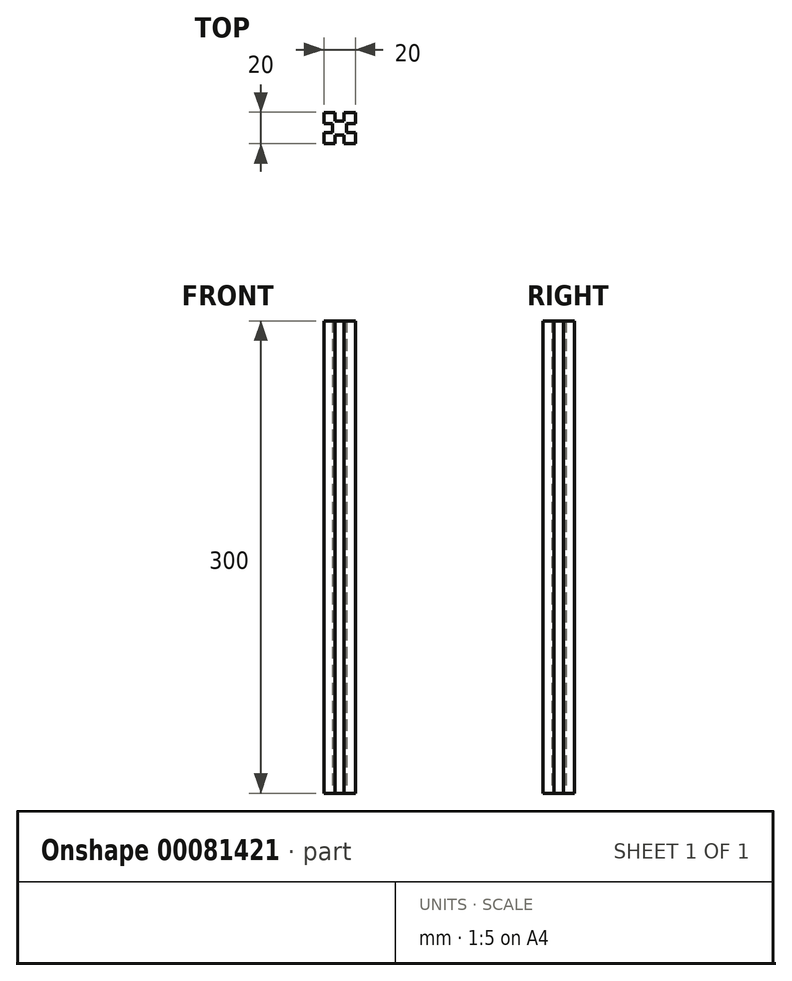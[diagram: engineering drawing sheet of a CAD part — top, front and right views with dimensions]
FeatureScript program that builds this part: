
annotation { "Feature Type Name" : "Feature", "Feature Type Description" : "" }
export const myFeature = defineFeature(function(context is Context, id is Id, definition is map)
    precondition{}
    {
        {
            var Q0;
            Q0=qCreatedBy(makeId("Top.planeOp"),FACE);
            var sketch = newSketch(context, id + "F0", { "sketchPlane" : qUnion([Q0])});
            skLineSegment(sketch, "E0.bottom", {"start": v(-87.17, -55.96) * mm, "end": v(-67.17, -55.96) * mm});
            skLineSegment(sketch, "E0.top", {"start": v(-87.17, -35.96) * mm, "end": v(-67.17, -35.96) * mm});
            skLineSegment(sketch, "E0.left", {"start": v(-87.17, -55.96) * mm, "end": v(-87.17, -35.96) * mm});
            skLineSegment(sketch, "E0.right", {"start": v(-67.17, -55.96) * mm, "end": v(-67.17, -35.96) * mm});
            skLineSegment(sketch, "E1.bottom", {"start": v(-80.17, -35.96) * mm, "end": v(-74.17, -35.96) * mm});
            skLineSegment(sketch, "E1.top", {"start": v(-80.17, -41.46) * mm, "end": v(-74.17, -41.46) * mm});
            skLineSegment(sketch, "E1.left", {"start": v(-80.17, -35.96) * mm, "end": v(-80.17, -41.46) * mm});
            skLineSegment(sketch, "E1.right", {"start": v(-74.17, -35.96) * mm, "end": v(-74.17, -41.46) * mm});
            skLineSegment(sketch, "E2.bottom", {"start": v(-67.17, -42.96) * mm, "end": v(-72.67, -42.96) * mm});
            skLineSegment(sketch, "E2.top", {"start": v(-67.17, -48.96) * mm, "end": v(-72.67, -48.96) * mm});
            skLineSegment(sketch, "E2.left", {"start": v(-67.17, -42.96) * mm, "end": v(-67.17, -48.96) * mm});
            skLineSegment(sketch, "E2.right", {"start": v(-72.67, -42.96) * mm, "end": v(-72.67, -48.96) * mm});
            skLineSegment(sketch, "E3.bottom", {"start": v(-74.17, -55.96) * mm, "end": v(-80.17, -55.96) * mm});
            skLineSegment(sketch, "E3.top", {"start": v(-74.17, -50.46) * mm, "end": v(-80.17, -50.46) * mm});
            skLineSegment(sketch, "E3.left", {"start": v(-74.17, -55.96) * mm, "end": v(-74.17, -50.46) * mm});
            skLineSegment(sketch, "E3.right", {"start": v(-80.17, -55.96) * mm, "end": v(-80.17, -50.46) * mm});
            skLineSegment(sketch, "E4.bottom", {"start": v(-87.17, -48.96) * mm, "end": v(-81.67, -48.96) * mm});
            skLineSegment(sketch, "E4.top", {"start": v(-87.17, -42.96) * mm, "end": v(-81.67, -42.96) * mm});
            skLineSegment(sketch, "E4.left", {"start": v(-87.17, -48.96) * mm, "end": v(-87.17, -42.96) * mm});
            skLineSegment(sketch, "E4.right", {"start": v(-81.67, -48.96) * mm, "end": v(-81.67, -42.96) * mm});
            skSolve(sketch);
        }
        {
            var Q0;
            Q0=makeQuery(id+"F0.imprint","IMPRINT",FACE,{"disambiguationData":[TD([[makeQuery(id+"F0.imprint","IMPRINT",EDGE,{"derivedFrom":sQuery(id+"F0.wireOp",EDGE,"E1.top")}),-1.0]])]});
            extrude(context, id + "F1", {"entities" : qUnion([Q0]), "depth" : 300 * mm});
        }
    });
